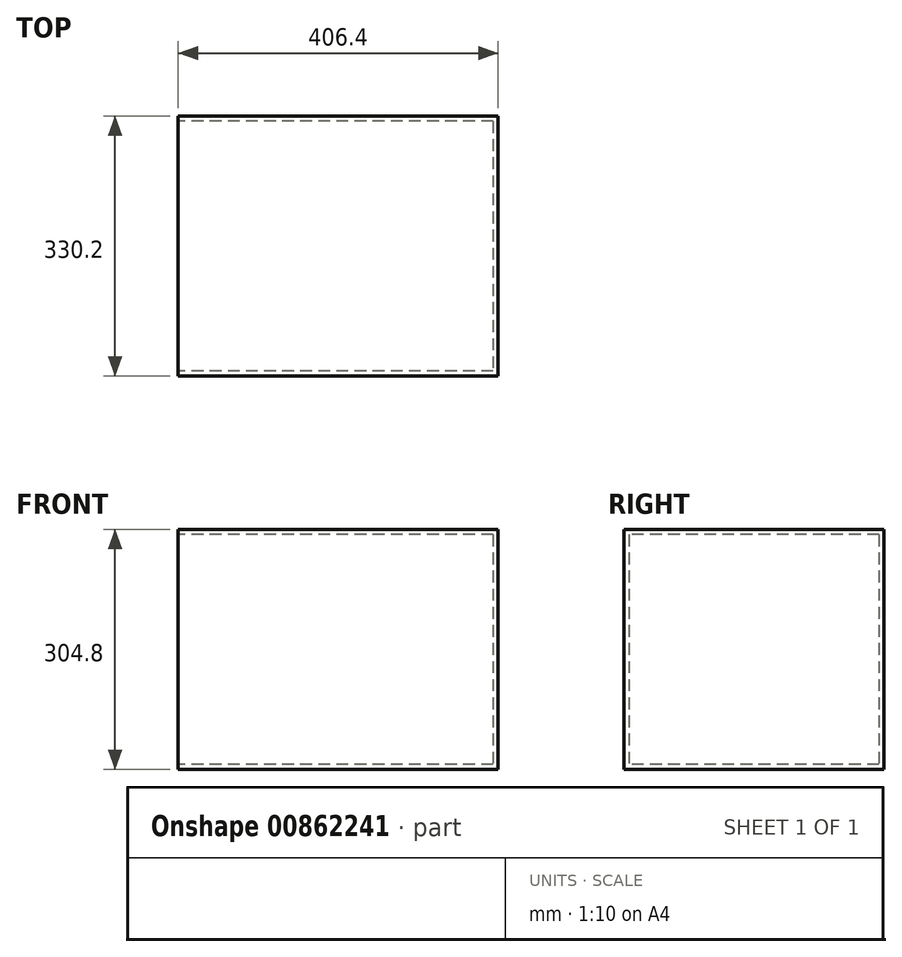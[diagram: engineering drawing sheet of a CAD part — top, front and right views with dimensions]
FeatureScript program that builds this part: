
annotation { "Feature Type Name" : "Feature", "Feature Type Description" : "" }
export const myFeature = defineFeature(function(context is Context, id is Id, definition is map)
    precondition{}
    {
        {
            var Q0;
            Q0=qCreatedBy(makeId("Top.planeOp"),FACE);
            var sketch = newSketch(context, id + "F0", { "sketchPlane" : qUnion([Q0])});
            skLineSegment(sketch, "E0.bottom", {"start": v(203.2, 165.1) * mm, "end": v(-203.2, 165.1) * mm});
            skLineSegment(sketch, "E0.top", {"start": v(203.2, -165.1) * mm, "end": v(-203.2, -165.1) * mm});
            skLineSegment(sketch, "E0.left", {"start": v(203.2, 165.1) * mm, "end": v(203.2, -165.1) * mm});
            skLineSegment(sketch, "E0.right", {"start": v(-203.2, 165.1) * mm, "end": v(-203.2, -165.1) * mm});
            skPoint(sketch, "E0.middle", {"position": v(0, 0) * mm});
            skSolve(sketch);
        }
        {
            var Q0;
            Q0=makeQuery(id+"F0.imprint","IMPRINT",FACE,{"disambiguationData":[TD([[makeQuery(id+"F0.imprint","IMPRINT",EDGE,{"derivedFrom":sQuery(id+"F0.wireOp",EDGE,"E0.bottom")}),1.0]])]});
            extrude(context, id + "F1", {"entities" : qUnion([Q0]), "depth" : 304.8 * mm, "offsetDistance" : 25.4 * mm});
        }
        {
            var Q0;
            Q0=makeQuery(id+"F1.opExtrude","SWEPT_FACE",FACE,{"disambiguationData":[OSD([sQuery(id+"F0.wireOp",EDGE,"E0.right")])]});
            shell(context, id + "F2", {"entities" : qUnion([Q0]), "thickness" : 6.35 * mm});
        }
    });
